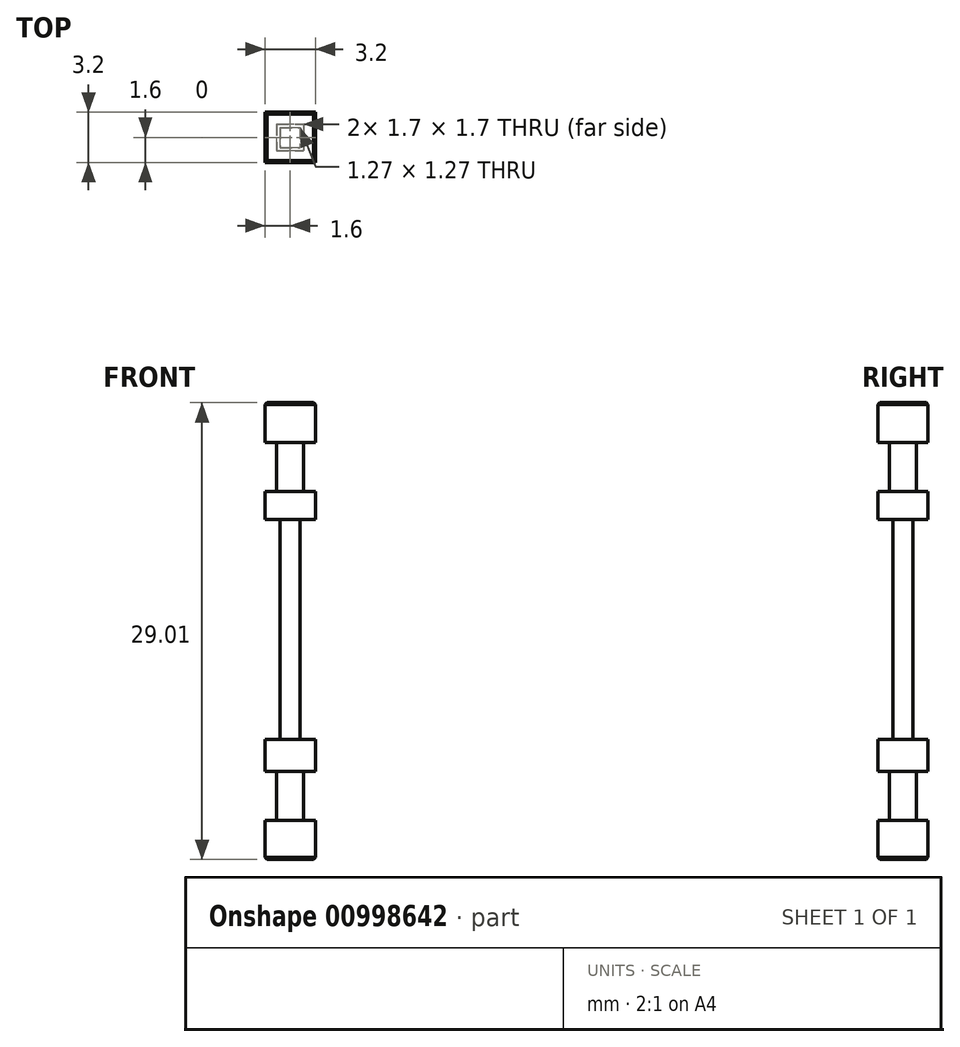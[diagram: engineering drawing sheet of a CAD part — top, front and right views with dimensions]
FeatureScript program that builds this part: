
annotation { "Feature Type Name" : "Feature", "Feature Type Description" : "" }
export const myFeature = defineFeature(function(context is Context, id is Id, definition is map)
    precondition{}
    {
        {
            var Q0;
            Q0=qCreatedBy(makeId("Top.planeOp"),FACE);
            var sketch = newSketch(context, id + "F0", { "sketchPlane" : qUnion([Q0])});
            skLineSegment(sketch, "E0.bottom", {"start": v(0, 0) * mm, "end": v(3.2, 0) * mm});
            skLineSegment(sketch, "E0.top", {"start": v(0, 3.2) * mm, "end": v(3.2, 3.2) * mm});
            skLineSegment(sketch, "E0.left", {"start": v(0, 0) * mm, "end": v(0, 3.2) * mm});
            skLineSegment(sketch, "E0.right", {"start": v(3.2, 0) * mm, "end": v(3.2, 3.2) * mm});
            skSolve(sketch);
        }
        {
            var Q0;
            Q0=qSketchRegion(id+"F0",true);
            extrude(context, id + "F1", {"entities" : qUnion([Q0]), "depth" : 2.5 * mm, "offsetDistance" : 25.4 * mm});
        }
        {
            var Q0;
            Q0=makeQuery(id+"F1.opExtrude","CAP_FACE",FACE,{"disambiguationData":[OSD([sQuery(id+"F0.wireOp",EDGE,"E0.bottom"),sQuery(id+"F0.wireOp",EDGE,"E0.top"),sQuery(id+"F0.wireOp",EDGE,"E0.left"),sQuery(id+"F0.wireOp",EDGE,"E0.right")])],"isStart":false});
            var sketch = newSketch(context, id + "F2", { "sketchPlane" : qUnion([Q0])});
            skLineSegment(sketch, "E1.bottom", {"start": v(0.75, 2.45) * mm, "end": v(2.45, 2.45) * mm});
            skLineSegment(sketch, "E1.top", {"start": v(0.75, 0.75) * mm, "end": v(2.45, 0.75) * mm});
            skLineSegment(sketch, "E1.left", {"start": v(0.75, 2.45) * mm, "end": v(0.75, 0.75) * mm});
            skLineSegment(sketch, "E1.right", {"start": v(2.45, 2.45) * mm, "end": v(2.45, 0.75) * mm});
            skSolve(sketch);
        }
        {
            var Q0;
            Q0=qSketchRegion(id+"F2",true);
            extrude(context, id + "F3", {"entities" : qUnion([Q0]), "operationType" : NewBodyOperationType.ADD, "depth" : 3.1 * mm, "offsetDistance" : 25.4 * mm});
        }
        {
            var Q0;
            Q0=makeQuery(id+"F3.opExtrude","CAP_FACE",FACE,{"disambiguationData":[OSD([sQuery(id+"F2.wireOp",EDGE,"E1.bottom"),sQuery(id+"F2.wireOp",EDGE,"E1.top"),sQuery(id+"F2.wireOp",EDGE,"E1.left"),sQuery(id+"F2.wireOp",EDGE,"E1.right")])],"isStart":false});
            var sketch = newSketch(context, id + "F4", { "sketchPlane" : qUnion([Q0])});
            skLineSegment(sketch, "E2.bottom", {"start": v(0, 0) * mm, "end": v(3.2, 0) * mm});
            skLineSegment(sketch, "E2.top", {"start": v(0, 3.2) * mm, "end": v(3.2, 3.2) * mm});
            skLineSegment(sketch, "E2.left", {"start": v(0, 0) * mm, "end": v(0, 3.2) * mm});
            skLineSegment(sketch, "E2.right", {"start": v(3.2, 0) * mm, "end": v(3.2, 3.2) * mm});
            skSolve(sketch);
        }
        {
            var Q0;
            Q0=makeQuery(id+"F4.imprint","IMPRINT",FACE,{"disambiguationData":[TD([[makeQuery(id+"F4.imprint","IMPRINT",EDGE,{"derivedFrom":makeQuery(id+"F3.opExtrude","CAP_EDGE",EDGE,{"disambiguationData":[OSD([sQuery(id+"F2.wireOp",EDGE,"E1.bottom")])],"isStart":false})}),-1.0]])]});
            var Q1;
            Q1=makeQuery(id+"F4.imprint","IMPRINT",FACE,{"disambiguationData":[TD([[makeQuery(id+"F4.imprint","IMPRINT",EDGE,{"derivedFrom":sQuery(id+"F4.wireOp",EDGE,"E2.bottom")}),1.0]])]});
            extrude(context, id + "F5", {"entities" : qUnion([Q0, Q1]), "operationType" : NewBodyOperationType.ADD, "depth" : 2.03 * mm, "offsetDistance" : 25.4 * mm});
        }
        {
            var Q0;
            Q0=makeQuery(id+"F5.opExtrude","CAP_FACE",FACE,{"disambiguationData":[OSD([sQuery(id+"F4.wireOp",EDGE,"E2.bottom"),sQuery(id+"F4.wireOp",EDGE,"E2.top"),sQuery(id+"F4.wireOp",EDGE,"E2.left"),sQuery(id+"F4.wireOp",EDGE,"E2.right")])],"isStart":false});
            var sketch = newSketch(context, id + "F6", { "sketchPlane" : qUnion([Q0])});
            skLineSegment(sketch, "E3.bottom", {"start": v(0.97, 2.24) * mm, "end": v(2.24, 2.24) * mm});
            skLineSegment(sketch, "E3.top", {"start": v(0.97, 0.97) * mm, "end": v(2.24, 0.97) * mm});
            skLineSegment(sketch, "E3.left", {"start": v(0.97, 2.24) * mm, "end": v(0.97, 0.97) * mm});
            skLineSegment(sketch, "E3.right", {"start": v(2.24, 2.24) * mm, "end": v(2.24, 0.97) * mm});
            skSolve(sketch);
        }
        {
            var Q0;
            Q0=qSketchRegion(id+"F6",true);
            extrude(context, id + "F7", {"entities" : qUnion([Q0]), "operationType" : NewBodyOperationType.ADD, "depth" : 13.97 * mm, "offsetDistance" : 25.4 * mm});
        }
        {
            var Q0;
            Q0=makeQuery(id+"F7.opExtrude","CAP_FACE",FACE,{"disambiguationData":[OSD([sQuery(id+"F6.wireOp",EDGE,"E3.bottom"),sQuery(id+"F6.wireOp",EDGE,"E3.top"),sQuery(id+"F6.wireOp",EDGE,"E3.left"),sQuery(id+"F6.wireOp",EDGE,"E3.right")])],"isStart":false});
            var sketch = newSketch(context, id + "F8", { "sketchPlane" : qUnion([Q0])});
            skLineSegment(sketch, "E4.bottom", {"start": v(0, 0) * mm, "end": v(3.2, 0) * mm});
            skLineSegment(sketch, "E4.top", {"start": v(0, 3.2) * mm, "end": v(3.2, 3.2) * mm});
            skLineSegment(sketch, "E4.left", {"start": v(0, 0) * mm, "end": v(0, 3.2) * mm});
            skLineSegment(sketch, "E4.right", {"start": v(3.2, 0) * mm, "end": v(3.2, 3.2) * mm});
            skSolve(sketch);
        }
        {
            var Q0;
            Q0=makeQuery(id+"F8.imprint","IMPRINT",FACE,{"disambiguationData":[TD([[makeQuery(id+"F8.imprint","IMPRINT",EDGE,{"derivedFrom":makeQuery(id+"F7.opExtrude","CAP_EDGE",EDGE,{"disambiguationData":[OSD([sQuery(id+"F6.wireOp",EDGE,"E3.bottom")])],"isStart":false})}),-1.0]])]});
            var Q1;
            Q1=makeQuery(id+"F8.imprint","IMPRINT",FACE,{"disambiguationData":[TD([[makeQuery(id+"F8.imprint","IMPRINT",EDGE,{"derivedFrom":sQuery(id+"F8.wireOp",EDGE,"E4.bottom")}),1.0]])]});
            extrude(context, id + "F9", {"entities" : qUnion([Q0, Q1]), "operationType" : NewBodyOperationType.ADD, "depth" : 1.78 * mm, "offsetDistance" : 25.4 * mm});
        }
        {
            var Q0;
            Q0=makeQuery(id+"F9.opExtrude","CAP_FACE",FACE,{"disambiguationData":[OSD([sQuery(id+"F8.wireOp",EDGE,"E4.bottom"),sQuery(id+"F8.wireOp",EDGE,"E4.top"),sQuery(id+"F8.wireOp",EDGE,"E4.left"),sQuery(id+"F8.wireOp",EDGE,"E4.right")])],"isStart":false});
            var sketch = newSketch(context, id + "F10", { "sketchPlane" : qUnion([Q0])});
            skLineSegment(sketch, "E5.bottom", {"start": v(0.75, 2.45) * mm, "end": v(2.45, 2.45) * mm});
            skLineSegment(sketch, "E5.top", {"start": v(0.75, 0.75) * mm, "end": v(2.45, 0.75) * mm});
            skLineSegment(sketch, "E5.left", {"start": v(0.75, 2.45) * mm, "end": v(0.75, 0.75) * mm});
            skLineSegment(sketch, "E5.right", {"start": v(2.45, 2.45) * mm, "end": v(2.45, 0.75) * mm});
            skSolve(sketch);
        }
        {
            var Q0;
            Q0=makeQuery(id+"F10.imprint","IMPRINT",FACE,{"disambiguationData":[TD([[makeQuery(id+"F10.imprint","IMPRINT",EDGE,{"derivedFrom":sQuery(id+"F10.wireOp",EDGE,"E5.bottom")}),-1.0]])]});
            extrude(context, id + "F11", {"entities" : qUnion([Q0]), "operationType" : NewBodyOperationType.ADD, "depth" : 3.12 * mm, "offsetDistance" : 25.4 * mm});
        }
        {
            var Q0;
            Q0=makeQuery(id+"F11.opExtrude","CAP_FACE",FACE,{"disambiguationData":[OSD([sQuery(id+"F10.wireOp",EDGE,"E5.bottom"),sQuery(id+"F10.wireOp",EDGE,"E5.top"),sQuery(id+"F10.wireOp",EDGE,"E5.left"),sQuery(id+"F10.wireOp",EDGE,"E5.right")])],"isStart":false});
            var sketch = newSketch(context, id + "F12", { "sketchPlane" : qUnion([Q0])});
            skLineSegment(sketch, "E6.bottom", {"start": v(0, 0) * mm, "end": v(3.2, 0) * mm});
            skLineSegment(sketch, "E6.top", {"start": v(0, 3.2) * mm, "end": v(3.2, 3.2) * mm});
            skLineSegment(sketch, "E6.left", {"start": v(0, 0) * mm, "end": v(0, 3.2) * mm});
            skLineSegment(sketch, "E6.right", {"start": v(3.2, 0) * mm, "end": v(3.2, 3.2) * mm});
            skSolve(sketch);
        }
        {
            var Q0;
            Q0=makeQuery(id+"F12.imprint","IMPRINT",FACE,{"disambiguationData":[TD([[makeQuery(id+"F12.imprint","IMPRINT",EDGE,{"derivedFrom":makeQuery(id+"F11.opExtrude","CAP_EDGE",EDGE,{"disambiguationData":[OSD([sQuery(id+"F10.wireOp",EDGE,"E5.bottom")])],"isStart":false})}),-1.0]])]});
            var Q1;
            Q1=makeQuery(id+"F12.imprint","IMPRINT",FACE,{"disambiguationData":[TD([[makeQuery(id+"F12.imprint","IMPRINT",EDGE,{"derivedFrom":sQuery(id+"F12.wireOp",EDGE,"E6.bottom")}),1.0]])]});
            extrude(context, id + "F13", {"entities" : qUnion([Q0, Q1]), "operationType" : NewBodyOperationType.ADD, "depth" : 2.5 * mm, "offsetDistance" : 25.4 * mm});
        }
        {
            var Q0;
            Q0=makeQuery(id+"F11.opExtrude","CAP_EDGE",EDGE,{"disambiguationData":[OSD([sQuery(id+"F10.wireOp",EDGE,"E5.left")])],"isStart":true});
            var Q1;
            Q1=makeQuery(id+"F11.opExtrude","CAP_EDGE",EDGE,{"disambiguationData":[OSD([sQuery(id+"F10.wireOp",EDGE,"E5.top")])],"isStart":true});
            var Q2;
            Q2=makeQuery(id+"F13.opExtrude","CAP_EDGE",EDGE,{"disambiguationData":[OSD([sQuery(id+"F12.wireOp",EDGE,"E6.left")])],"isStart":false});
            var Q3;
            Q3=makeQuery(id+"F13.opExtrude","CAP_EDGE",EDGE,{"disambiguationData":[OSD([sQuery(id+"F12.wireOp",EDGE,"E6.top")])],"isStart":false});
            var Q4;
            Q4=makeQuery(id+"F13.opExtrude","CAP_EDGE",EDGE,{"disambiguationData":[OSD([sQuery(id+"F12.wireOp",EDGE,"E6.right")])],"isStart":false});
            var Q5;
            Q5=makeQuery(id+"F13.opExtrude","CAP_EDGE",EDGE,{"disambiguationData":[OSD([sQuery(id+"F12.wireOp",EDGE,"E6.bottom")])],"isStart":false});
            var Q6;
            Q6=makeQuery(id+"F7.opExtrude","CAP_EDGE",EDGE,{"disambiguationData":[OSD([sQuery(id+"F6.wireOp",EDGE,"E3.left")])],"isStart":true});
            var Q7;
            Q7=makeQuery(id+"F7.opExtrude","CAP_EDGE",EDGE,{"disambiguationData":[OSD([sQuery(id+"F6.wireOp",EDGE,"E3.top")])],"isStart":true});
            var Q8;
            Q8=makeQuery(id+"F3.opExtrude","CAP_EDGE",EDGE,{"disambiguationData":[OSD([sQuery(id+"F2.wireOp",EDGE,"E1.left")])],"isStart":true});
            var Q9;
            Q9=makeQuery(id+"F3.opExtrude","CAP_EDGE",EDGE,{"disambiguationData":[OSD([sQuery(id+"F2.wireOp",EDGE,"E1.top")])],"isStart":true});
            var Q10;
            Q10=makeQuery(id+"F1.opExtrude","CAP_EDGE",EDGE,{"disambiguationData":[OSD([sQuery(id+"F0.wireOp",EDGE,"E0.left")])],"isStart":true});
            var Q11;
            Q11=makeQuery(id+"F1.opExtrude","CAP_EDGE",EDGE,{"disambiguationData":[OSD([sQuery(id+"F0.wireOp",EDGE,"E0.bottom")])],"isStart":true});
            var Q12;
            Q12=makeQuery(id+"F11.opExtrude","CAP_EDGE",EDGE,{"disambiguationData":[OSD([sQuery(id+"F10.wireOp",EDGE,"E5.left")])],"isStart":false});
            var Q13;
            Q13=makeQuery(id+"F11.opExtrude","CAP_EDGE",EDGE,{"disambiguationData":[OSD([sQuery(id+"F10.wireOp",EDGE,"E5.top")])],"isStart":false});
            var Q14;
            Q14=makeQuery(id+"F7.opExtrude","CAP_EDGE",EDGE,{"disambiguationData":[OSD([sQuery(id+"F6.wireOp",EDGE,"E3.left")])],"isStart":false});
            var Q15;
            Q15=makeQuery(id+"F7.opExtrude","CAP_EDGE",EDGE,{"disambiguationData":[OSD([sQuery(id+"F6.wireOp",EDGE,"E3.top")])],"isStart":false});
            var Q16;
            Q16=makeQuery(id+"F3.opExtrude","CAP_EDGE",EDGE,{"disambiguationData":[OSD([sQuery(id+"F2.wireOp",EDGE,"E1.left")])],"isStart":false});
            var Q17;
            Q17=makeQuery(id+"F3.opExtrude","CAP_EDGE",EDGE,{"disambiguationData":[OSD([sQuery(id+"F2.wireOp",EDGE,"E1.top")])],"isStart":false});
            var Q18;
            Q18=makeQuery(id+"F1.opExtrude","CAP_EDGE",EDGE,{"disambiguationData":[OSD([sQuery(id+"F0.wireOp",EDGE,"E0.right")])],"isStart":true});
            var Q19;
            Q19=makeQuery(id+"F1.opExtrude","CAP_EDGE",EDGE,{"disambiguationData":[OSD([sQuery(id+"F0.wireOp",EDGE,"E0.top")])],"isStart":true});
            var Q20;
            Q20=makeQuery(id+"F11.opExtrude","CAP_EDGE",EDGE,{"disambiguationData":[OSD([sQuery(id+"F10.wireOp",EDGE,"E5.right")])],"isStart":false});
            var Q21;
            Q21=makeQuery(id+"F11.opExtrude","CAP_EDGE",EDGE,{"disambiguationData":[OSD([sQuery(id+"F10.wireOp",EDGE,"E5.bottom")])],"isStart":false});
            var Q22;
            Q22=makeQuery(id+"F7.opExtrude","CAP_EDGE",EDGE,{"disambiguationData":[OSD([sQuery(id+"F6.wireOp",EDGE,"E3.right")])],"isStart":false});
            var Q23;
            Q23=makeQuery(id+"F7.opExtrude","CAP_EDGE",EDGE,{"disambiguationData":[OSD([sQuery(id+"F6.wireOp",EDGE,"E3.bottom")])],"isStart":false});
            var Q24;
            Q24=makeQuery(id+"F3.opExtrude","CAP_EDGE",EDGE,{"disambiguationData":[OSD([sQuery(id+"F2.wireOp",EDGE,"E1.right")])],"isStart":false});
            var Q25;
            Q25=makeQuery(id+"F3.opExtrude","CAP_EDGE",EDGE,{"disambiguationData":[OSD([sQuery(id+"F2.wireOp",EDGE,"E1.bottom")])],"isStart":false});
            var Q26;
            Q26=makeQuery(id+"F11.opExtrude","CAP_EDGE",EDGE,{"disambiguationData":[OSD([sQuery(id+"F10.wireOp",EDGE,"E5.right")])],"isStart":true});
            var Q27;
            Q27=makeQuery(id+"F11.opExtrude","CAP_EDGE",EDGE,{"disambiguationData":[OSD([sQuery(id+"F10.wireOp",EDGE,"E5.bottom")])],"isStart":true});
            var Q28;
            Q28=makeQuery(id+"F7.opExtrude","CAP_EDGE",EDGE,{"disambiguationData":[OSD([sQuery(id+"F6.wireOp",EDGE,"E3.right")])],"isStart":true});
            var Q29;
            Q29=makeQuery(id+"F7.opExtrude","CAP_EDGE",EDGE,{"disambiguationData":[OSD([sQuery(id+"F6.wireOp",EDGE,"E3.bottom")])],"isStart":true});
            var Q30;
            Q30=makeQuery(id+"F3.opExtrude","CAP_EDGE",EDGE,{"disambiguationData":[OSD([sQuery(id+"F2.wireOp",EDGE,"E1.right")])],"isStart":true});
            var Q31;
            Q31=makeQuery(id+"F3.opExtrude","CAP_EDGE",EDGE,{"disambiguationData":[OSD([sQuery(id+"F2.wireOp",EDGE,"E1.bottom")])],"isStart":true});
            chamfer(context, id + "F14", {"entities" : qUnion([Q0, Q1, Q2, Q3, Q4, Q5, Q6, Q7, Q8, Q9, Q10, Q11, Q12, Q13, Q14, Q15, Q16, Q17, Q18, Q19, Q20, Q21, Q22, Q23, Q24, Q25, Q26, Q27, Q28, Q29, Q30, Q31]), "chamferType" : ChamferType.OFFSET_ANGLE, "width" : 0.13 * mm, "oppositeDirection" : false, "angle" : 45 * degree, "tangentPropagation" : true});
        }
    });
